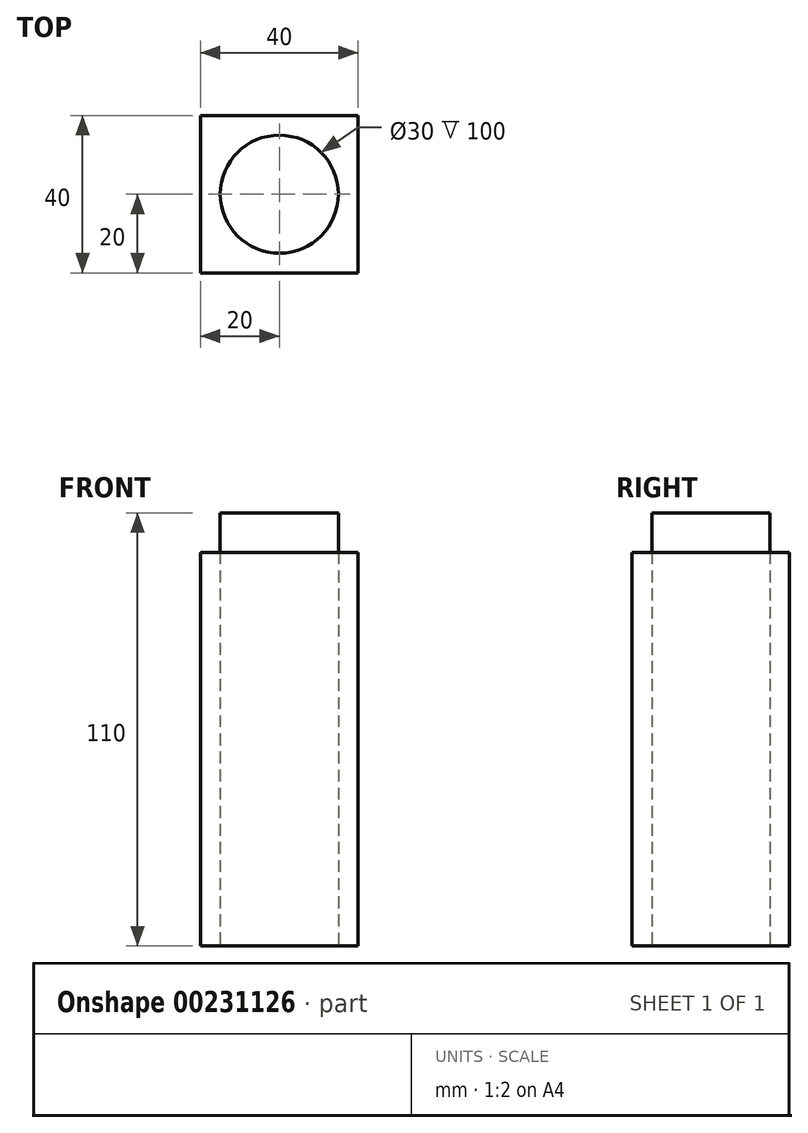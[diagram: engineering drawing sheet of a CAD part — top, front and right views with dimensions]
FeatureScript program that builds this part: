
annotation { "Feature Type Name" : "Feature", "Feature Type Description" : "" }
export const myFeature = defineFeature(function(context is Context, id is Id, definition is map)
    precondition{}
    {
        {
            var Q0;
            Q0=qCreatedBy(makeId("Top.planeOp"),FACE);
            var sketch = newSketch(context, id + "F0", { "sketchPlane" : qUnion([Q0])});
            skLineSegment(sketch, "E0.bottom", {"start": v(20, -20) * mm, "end": v(-20, -20) * mm});
            skLineSegment(sketch, "E0.top", {"start": v(20, 20) * mm, "end": v(-20, 20) * mm});
            skLineSegment(sketch, "E0.left", {"start": v(20, -20) * mm, "end": v(20, 20) * mm});
            skLineSegment(sketch, "E0.right", {"start": v(-20, -20) * mm, "end": v(-20, 20) * mm});
            skPoint(sketch, "E0.middle", {"position": v(0, 0) * mm});
            skCircle(sketch, "E1", {"center": v(0, 0) * mm, "radius": 15 * mm});
            skSolve(sketch);
        }
        {
            var Q0;
            Q0=makeQuery(id+"F0.imprint","IMPRINT",FACE,{"disambiguationData":[TD([[makeQuery(id+"F0.imprint","IMPRINT",EDGE,{"derivedFrom":sQuery(id+"F0.wireOp",EDGE,"E0.bottom")}),-1.0]])]});
            extrude(context, id + "F1", {"entities" : qUnion([Q0]), "depth" : 100 * mm});
        }
        {
            var Q0;
            Q0=qCreatedBy(makeId("Top.planeOp"),FACE);
            var sketch = newSketch(context, id + "F2", { "sketchPlane" : qUnion([Q0])});
            skCircle(sketch, "E2.0", {"center": v(0, 0) * mm, "radius": 15 * mm});
            skSolve(sketch);
        }
        {
            var Q0;
            Q0 = qSketchRegion(id + "F2", true);
            extrude(context, id + "F3", {"entities" : qUnion([Q0]), "depth" : 110 * mm});
        }
    });
